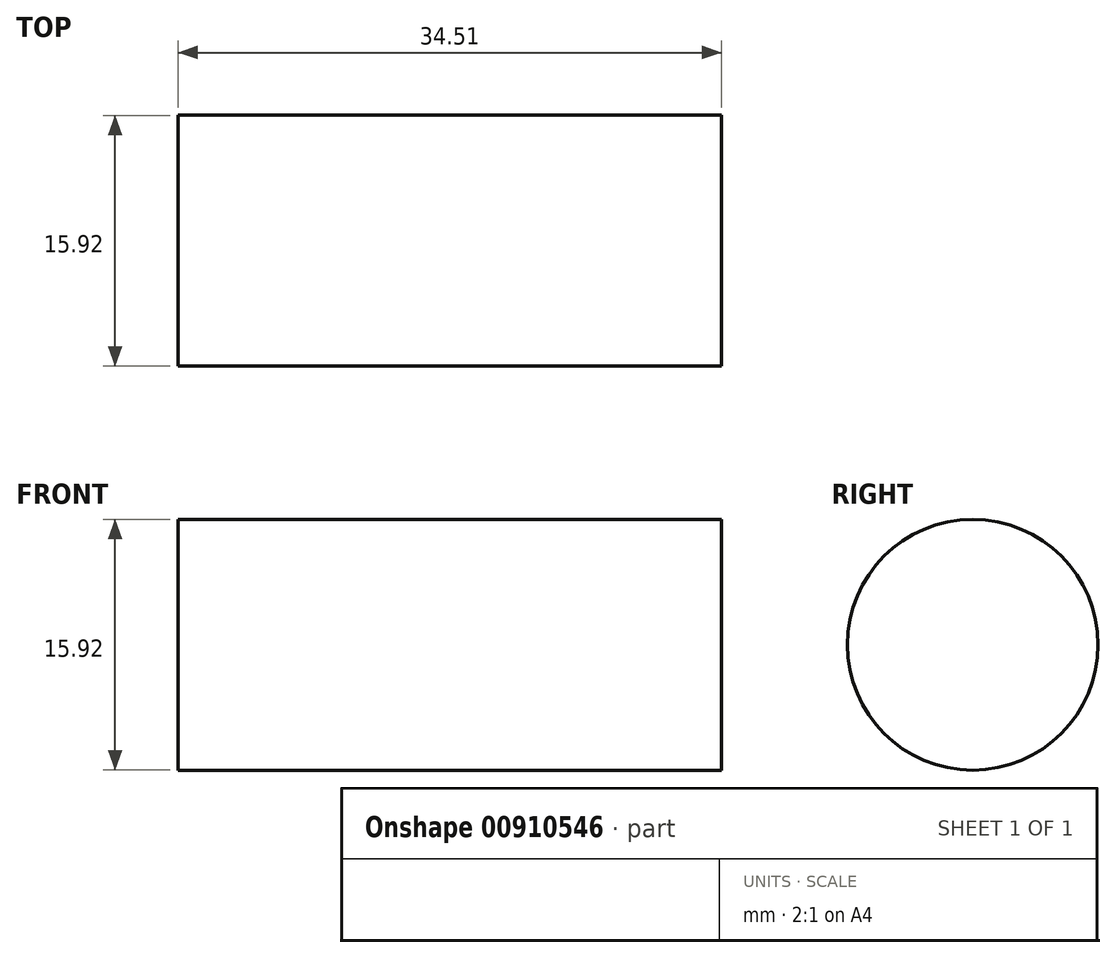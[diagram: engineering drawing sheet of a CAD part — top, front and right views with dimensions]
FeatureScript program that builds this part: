
annotation { "Feature Type Name" : "Feature", "Feature Type Description" : "" }
export const myFeature = defineFeature(function(context is Context, id is Id, definition is map)
    precondition{}
    {
        {
            var Q0;
            Q0=qCreatedBy(makeId("Top.planeOp"),FACE);
            var sketch = newSketch(context, id + "F0", { "sketchPlane" : qUnion([Q0])});
            skLineSegment(sketch, "E0", {"start": v(-59.7, 42.62) * mm, "end": v(-25.2, 42.62) * mm});
            skLineSegment(sketch, "E1", {"start": v(-25.2, 42.62) * mm, "end": v(-25.2, 34.66) * mm});
            skLineSegment(sketch, "E2", {"start": v(-25.2, 34.66) * mm, "end": v(-59.7, 34.66) * mm});
            skLineSegment(sketch, "E3", {"start": v(-59.7, 34.66) * mm, "end": v(-59.7, 42.62) * mm});
            skSolve(sketch);
        }
        {
            var Q0;
            Q0=makeQuery(id+"F0.imprint","IMPRINT",FACE,{"disambiguationData":[TD([[makeQuery(id+"F0.imprint","IMPRINT",EDGE,{"derivedFrom":sQuery(id+"F0.wireOp",EDGE,"E0")}),-1.0]])]});
            var Q1;
            Q1=sQuery(id+"F0.wireOp",EDGE,"E2");
            revolve(context, id + "F1", {"surfaceOperationType" : NewSurfaceOperationType.NEW, "entities" : qUnion([Q0]), "axis" : qUnion([Q1]), "revolveType" : RevolveType.FULL});
        }
    });
